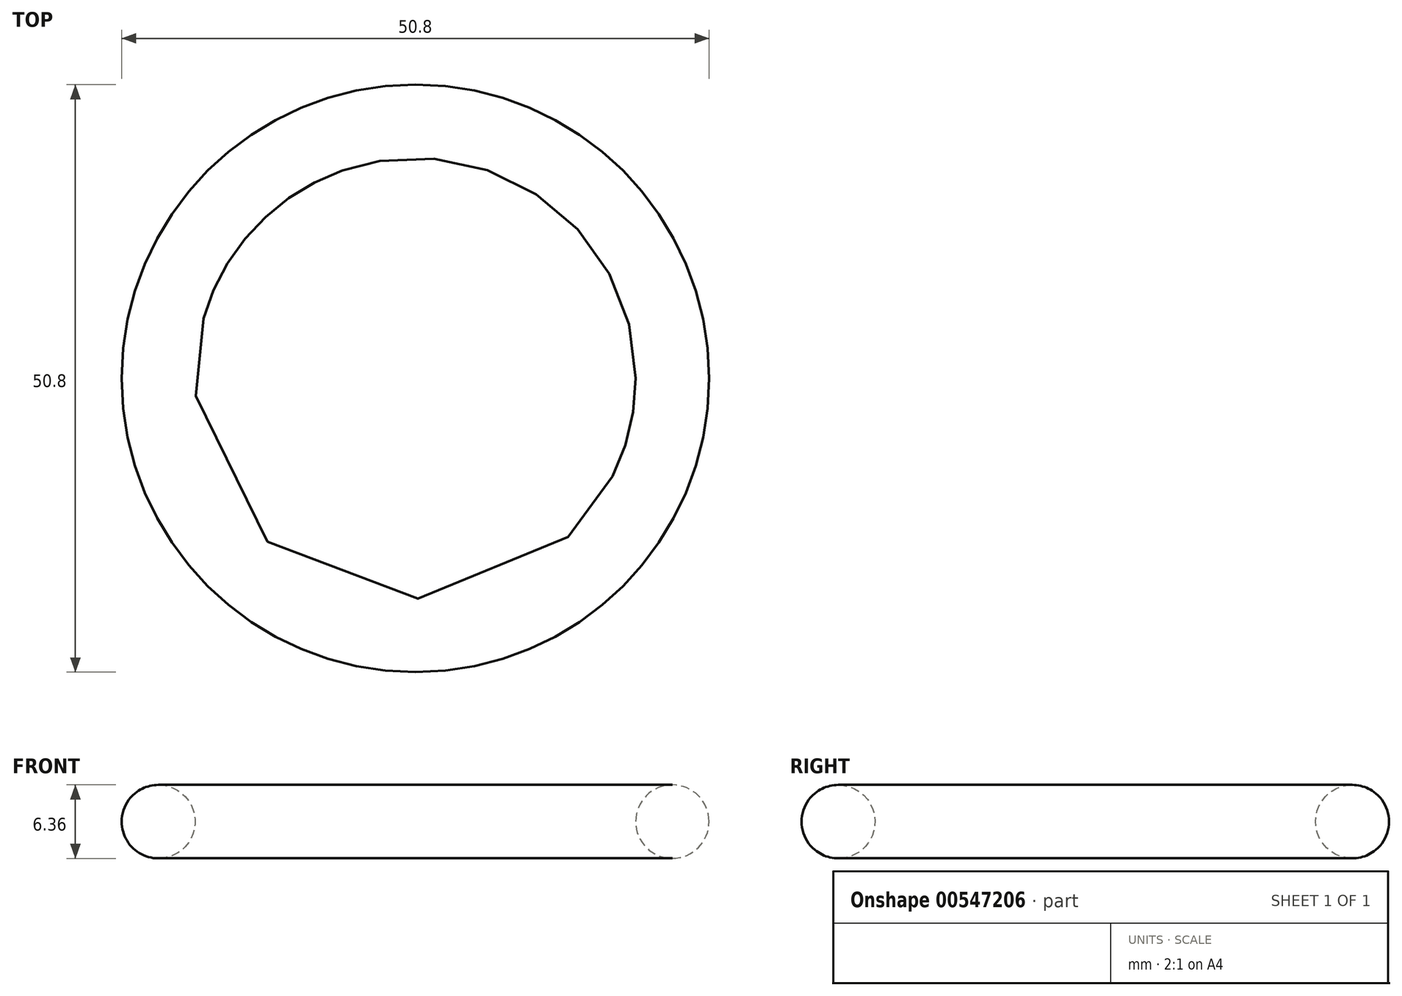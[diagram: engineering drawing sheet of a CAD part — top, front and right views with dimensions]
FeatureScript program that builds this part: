
annotation { "Feature Type Name" : "Feature", "Feature Type Description" : "" }
export const myFeature = defineFeature(function(context is Context, id is Id, definition is map)
    precondition{}
    {
        {
            var Q0;
            Q0=qCreatedBy(makeId("Front.planeOp"),FACE);
            var sketch = newSketch(context, id + "F0", { "sketchPlane" : qUnion([Q0])});
            skCircle(sketch, "E0", {"center": v(-22.22, 0) * mm, "radius": 3.18 * mm});
            skLineSegment(sketch, "E1", {"start": v(0, 33.77) * mm, "end": v(0, -27.4) * mm, "construction": true});
            skSolve(sketch);
        }
        {
            var Q0;
            Q0 = qSketchRegion(id + "F0", true);
            var Q1;
            Q1=sQuery(id+"F0.wireOp",EDGE,"E1");
            revolve(context, id + "F1", {"entities" : qUnion([Q0]), "axis" : qUnion([Q1]), "revolveType" : RevolveType.FULL});
        }
    });
